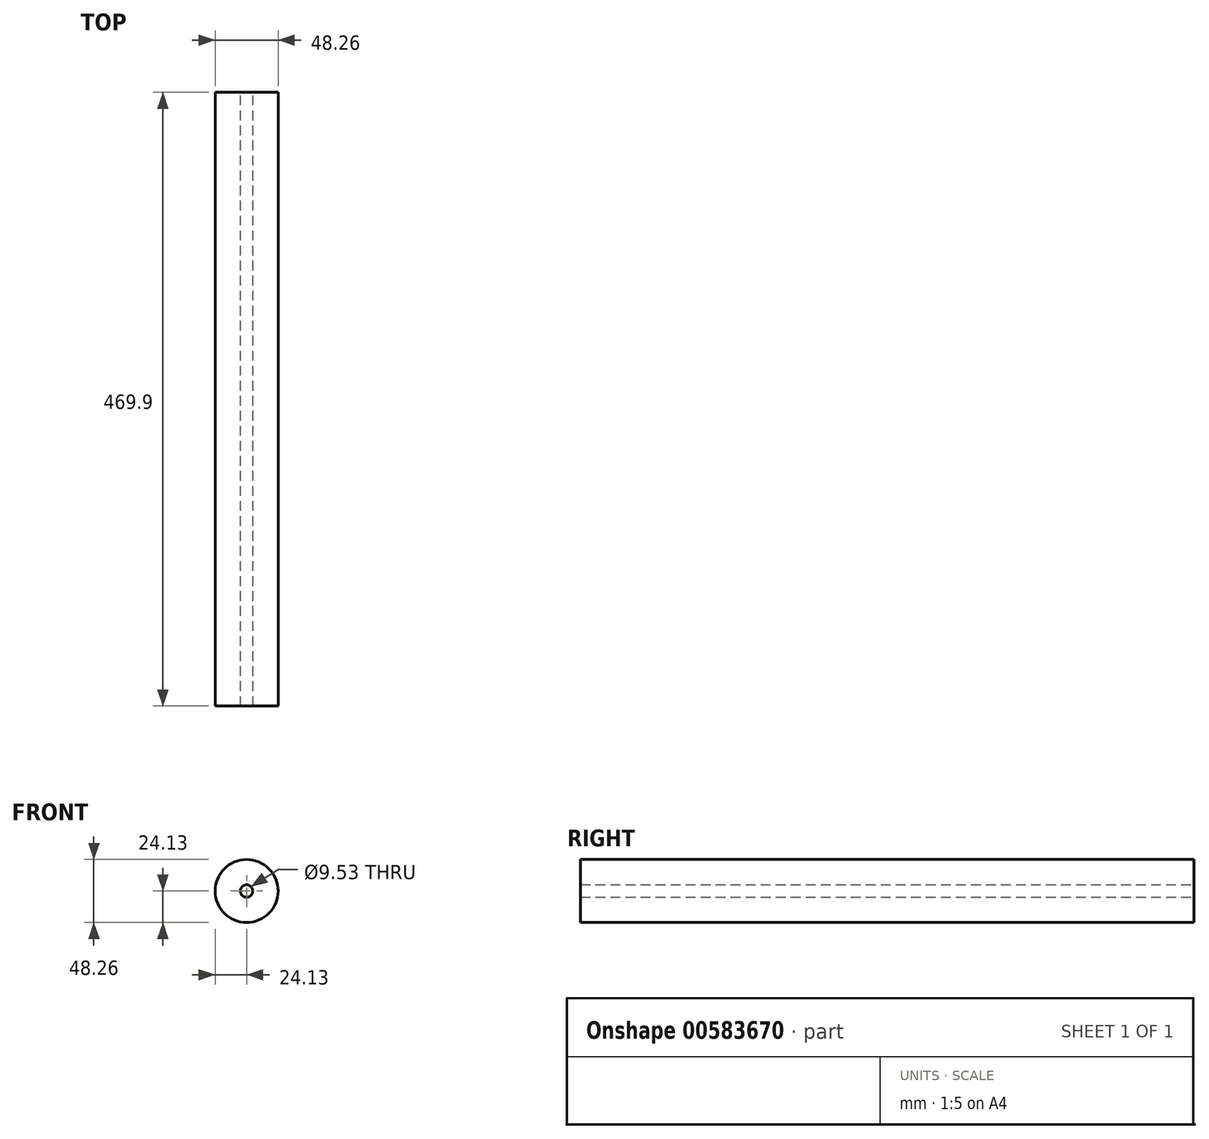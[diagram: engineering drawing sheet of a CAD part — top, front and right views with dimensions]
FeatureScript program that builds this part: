
annotation { "Feature Type Name" : "Feature", "Feature Type Description" : "" }
export const myFeature = defineFeature(function(context is Context, id is Id, definition is map)
    precondition{}
    {
        {
            var Q0;
            Q0=qCreatedBy(makeId("Front.planeOp"),FACE);
            var sketch = newSketch(context, id + "F0", { "sketchPlane" : qUnion([Q0])});
            skCircle(sketch, "E0", {"center": v(0, 0) * mm, "radius": 24.13 * mm});
            skCircle(sketch, "E1", {"center": v(0, 0) * mm, "radius": 4.76 * mm});
            skSolve(sketch);
        }
        {
            var Q0;
            Q0=makeQuery(id+"F0.imprint","IMPRINT",FACE,{"disambiguationData":[TD([[makeQuery(id+"F0.imprint","IMPRINT",EDGE,{"derivedFrom":sQuery(id+"F0.wireOp",EDGE,"E0")}),1.0]])]});
            extrude(context, id + "F1", {"entities" : qUnion([Q0]), "depth" : 469.9 * mm, "offsetDistance" : 25.4 * mm});
        }
    });
